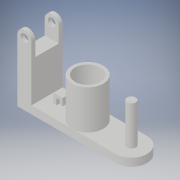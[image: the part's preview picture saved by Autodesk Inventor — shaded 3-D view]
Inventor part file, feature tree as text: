
AUTODESK INVENTOR PART (.ipt)
format: ipt  version: 2019 (Build 230136000, 136)  size: 190,464 bytes
history: native  units: in
note: dims shown in document units (in); Inventor stores cm internally (conversion verified against a paired STEP export)
features: extrude x7, sketch x6
ambient origin geometry x8: Origin, YZ Plane, XZ Plane, XY Plane, X Axis, Y Axis, Z Axis, Center Point
bodies: Solid1 (feature_tree)
feature tree (13):
  extrude  "Extrusion1"  Depth=0.1969in
  sketch  "Sketch2"  dims[d6=0.1772in d7=0.1969in]
  extrude  "Extrusion5"  Depth=0.1969in
  extrude  "Extrusion6"  Depth=0.3543in
  extrude  "Extrusion7"  Depth=0.7874in
  extrude  "Extrusion8"  Depth=0.7874in
  extrude  "Extrusion9"  Depth=0.3937in
  extrude  "Extrusion10"  Depth=0.1969in
  sketch  "Sketch1"  dims[d0=1.5748in d2=0.1969in]
  sketch  "Sketch7"  dims[d8=0.3543in d9=2.126in]
  sketch  "Sketch9"  dims[d10=0.7874in d11=0.0in d12=0.1181in]
  sketch  "Sketch10"  dims[d13=0.2559in d14=0.7874in]
  sketch  "Sketch12"  dims[d16=1.0236in d19=0.3937in d20=0.2205in d21=0.3937in d22=0.5984in d40=0.5512in d41=0.5512in d42=0.5906in d43=0.5512in d44=0.0in d47=1.2795in d48=0.9843in d49=0.0in d50=0.6299in d51=1.2205in d52=0.0in d53=0.2362in d54=0.1575in d55=0.315in d56=0.2362in d57=0.2362in d58=0.0in d59=0.0787in d60=0.0787in d61=0.1575in d62=0.0591in d63=0.1575in d64=0.0in d65=0.1969in d66=0.0in d67=0.0in]
